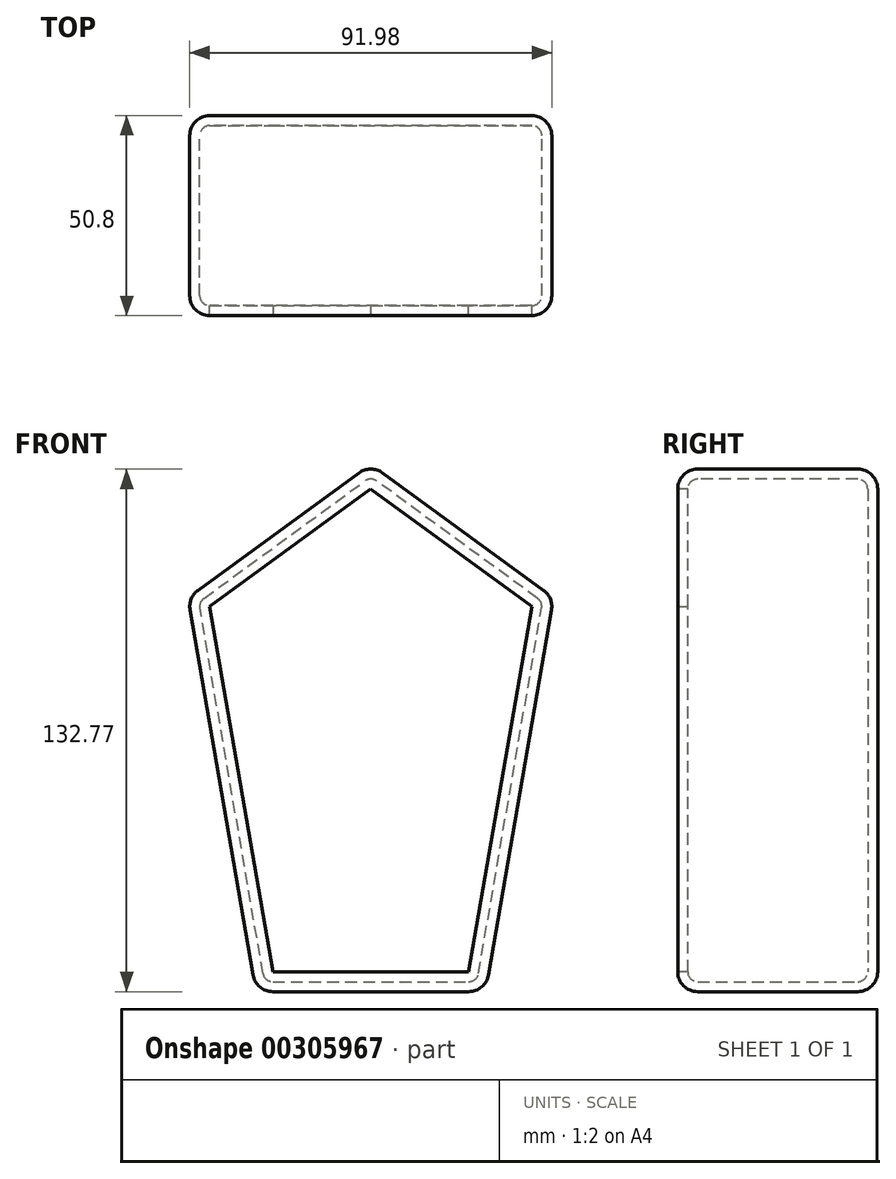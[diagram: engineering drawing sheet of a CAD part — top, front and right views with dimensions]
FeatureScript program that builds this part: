
annotation { "Feature Type Name" : "Feature", "Feature Type Description" : "" }
export const myFeature = defineFeature(function(context is Context, id is Id, definition is map)
    precondition{}
    {
        {
            var Q0;
            Q0=qCreatedBy(makeId("Front.planeOp"),FACE);
            var sketch = newSketch(context, id + "F0", { "sketchPlane" : qUnion([Q0])});
            skLineSegment(sketch, "E0", {"start": v(-29.16, -41) * mm, "end": v(21.64, -41) * mm});
            skLineSegment(sketch, "E1", {"start": v(-29.16, -41) * mm, "end": v(-46.45, 59.13) * mm});
            skLineSegment(sketch, "E2", {"start": v(-46.45, 59.13) * mm, "end": v(0, 92.99) * mm});
            skLineSegment(sketch, "E3.MirrorCS", {"start": v(46.45, 59.13) * mm, "end": v(0, 92.99) * mm});
            skLineSegment(sketch, "E4.MirrorCS", {"start": v(29.16, -41) * mm, "end": v(46.45, 59.13) * mm});
            skLineSegment(sketch, "E5.MirrorCS", {"start": v(29.16, -41) * mm, "end": v(-21.64, -41) * mm});
            skSolve(sketch);
        }
        {
            var Q0;
            {var subQ0=sQuery(id+"F0.wireOp",EDGE,"E0");Q0=makeQuery(id+"F0.imprint","IMPRINT",FACE,{"disambiguationData":[TD([[makeQuery(id+"F0.imprint","IMPRINT",EDGE,{"derivedFrom":subQ0}),1.0]])]});}
            extrude(context, id + "F1", {"entities" : qUnion([Q0]), "depth" : 50.8 * mm});
        }
        {
            var Q0;
            Q0=makeQuery(id+"F1.opExtrude","CAP_FACE",FACE,{"disambiguationData":[OSD([sQuery(id+"F0.wireOp",EDGE,"E0"),sQuery(id+"F0.wireOp",EDGE,"E1"),sQuery(id+"F0.wireOp",EDGE,"E2"),sQuery(id+"F0.wireOp",EDGE,"E3.MirrorCS"),sQuery(id+"F0.wireOp",EDGE,"E4.MirrorCS"),sQuery(id+"F0.wireOp",EDGE,"E5.MirrorCS")])],"isStart":false});
            var Q1;
            Q1=makeQuery(id+"F1.opExtrude","SWEPT_FACE",FACE,{"disambiguationData":[OSD([sQuery(id+"F0.wireOp",EDGE,"E4.MirrorCS")])]});
            var Q2;
            Q2=makeQuery(id+"F1.opExtrude","CAP_FACE",FACE,{"disambiguationData":[OSD([sQuery(id+"F0.wireOp",EDGE,"E0"),sQuery(id+"F0.wireOp",EDGE,"E1"),sQuery(id+"F0.wireOp",EDGE,"E2"),sQuery(id+"F0.wireOp",EDGE,"E3.MirrorCS"),sQuery(id+"F0.wireOp",EDGE,"E4.MirrorCS"),sQuery(id+"F0.wireOp",EDGE,"E5.MirrorCS")])],"isStart":true});
            var Q3;
            Q3=makeQuery(id+"F1.opExtrude","SWEPT_FACE",FACE,{"disambiguationData":[OSD([sQuery(id+"F0.wireOp",EDGE,"E1")])]});
            var Q4;
            Q4=makeQuery(id+"F1.opExtrude","SWEPT_FACE",FACE,{"disambiguationData":[OSD([sQuery(id+"F0.wireOp",EDGE,"E2")])]});
            fillet(context, id + "F2", {"entities" : qUnion([Q0, Q1, Q2, Q3, Q4]), "radius" : 5.08 * mm, "tangentPropagation" : true, "allowEdgeOverflow" : false});
        }
        {
            var Q0;
            Q0=makeQuery(id+"F1.opExtrude","CAP_FACE",FACE,{"disambiguationData":[OSD([sQuery(id+"F0.wireOp",EDGE,"E0"),sQuery(id+"F0.wireOp",EDGE,"E1"),sQuery(id+"F0.wireOp",EDGE,"E2"),sQuery(id+"F0.wireOp",EDGE,"E3.MirrorCS"),sQuery(id+"F0.wireOp",EDGE,"E4.MirrorCS"),sQuery(id+"F0.wireOp",EDGE,"E5.MirrorCS")])],"isStart":false});
            shell(context, id + "F3", {"entities" : qUnion([Q0]), "thickness" : 2.54 * mm});
        }
    });
